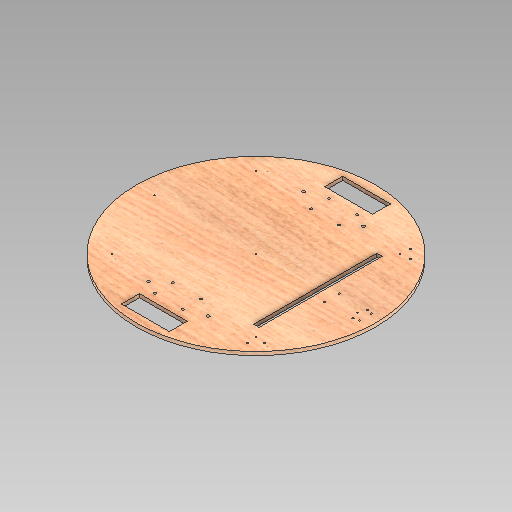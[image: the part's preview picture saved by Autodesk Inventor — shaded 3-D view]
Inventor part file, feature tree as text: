
AUTODESK INVENTOR PART (.ipt)
format: ipt  version: 2020 (Build 240168000, 168)  size: 377,856 bytes
history: native  units: in
note: dims shown in document units (in); Inventor stores cm internally (conversion verified against a paired STEP export)
features: extrude x5, sketch x4, pattern_circular x3
ambient origin geometry x8: Origin, YZ Plane, XZ Plane, XY Plane, X Axis, Y Axis, Z Axis, Center Point
bodies: Solid1 (feature_tree)
feature tree (12):
  extrude  "Extrusion1"  Depth=0.5906in
  extrude  "Extrusion2"  Depth=3.1496in
  pattern_circular  "Circular Pattern1"  Count=3  [1 undecoded]
  extrude  "Extrusion3"  Depth=3.1496in
  extrude  "Extrusion4"  Depth=0.3543in
  pattern_circular  "Circular Pattern2"  [2 undecoded]
  pattern_circular  "Circular Pattern3"  [2 undecoded]
  extrude  "Extrusion5"  Depth=0.3543in
  sketch  "Sketch1"  dims[d0=15.748in d2=0.5906in]
  sketch  "Sketch2"  dims[d3=1.5748in d4=3.1496in d5=1.1811in]
  sketch  "Sketch3"  dims[d6=3.1496in d7=0.3346in]
  sketch  "Sketch5"  dims[d8=0.6693in d9=1.0236in d10=2.0472in d15=0.1575in d16=0.1575in d17=0.1575in d18=0.1575in d19=0.2362in d20=0.0in d21=0.0787in d22=0.0787in d23=0.0787in d24=45.0deg d25=6.6929in d26=0.0787in d27=0.2362in d28=0.0in d29=3.1496in d30=360.0deg d35=1.8504in d36=1.1811in d37=0.7554in d38=0.4331in d39=0.1575in d40=1.8504in d41=1.1811in d42=4.3898in d43=0.7554in d44=0.4724in d45=1.8504in d46=0.9449in d47=0.1181in d48=0.1181in d49=0.1181in d50=0.1181in d51=0.2362in d52=0.0in d53=0.6693in d54=0.3937in d55=0.3937in d56=0.3937in d57=0.1181in d58=0.1181in d59=0.2362in d60=0.0in d61=0.7874in d62=45.0deg d64=0.7874in d65=45.0deg d68=5.1181in d69=10.2362in d70=0.3543in d71=8.1102in d73=1.1811in d74=1.7717in d75=2.7559in d76=2.7559in d77=0.3543in d78=0.0in d79=3.937in d80=10.2362in d81=0.1969in d82=0.1969in d83=0.1969in d84=0.1969in]
note: 5 required parameter values undecoded (feature->parameter linkage not recoverable at this tier; creation-order binding heuristic only, values carry confidence <= 0.55)
